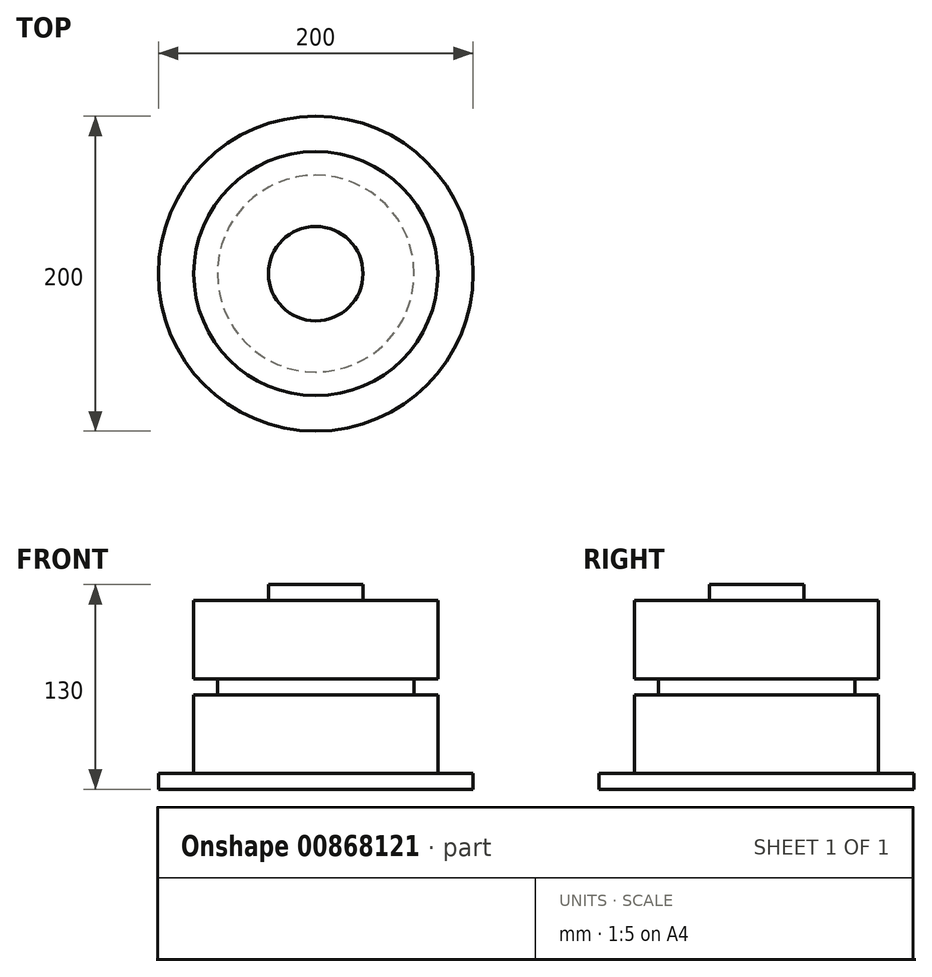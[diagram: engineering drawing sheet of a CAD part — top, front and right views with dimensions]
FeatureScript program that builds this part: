
annotation { "Feature Type Name" : "Feature", "Feature Type Description" : "" }
export const myFeature = defineFeature(function(context is Context, id is Id, definition is map)
    precondition{}
    {
        {
            var Q0;
            Q0=qCreatedBy(makeId("Front.planeOp"),FACE);
            var sketch = newSketch(context, id + "F0", { "sketchPlane" : qUnion([Q0])});
            skLineSegment(sketch, "E0", {"start": v(0, 0) * mm, "end": v(-30, 0) * mm});
            skLineSegment(sketch, "E1", {"start": v(-30, 0) * mm, "end": v(-30, -10) * mm});
            skLineSegment(sketch, "E2", {"start": v(-30, -10) * mm, "end": v(-77.5, -10) * mm});
            skLineSegment(sketch, "E3", {"start": v(-77.5, -10) * mm, "end": v(-77.5, -60) * mm});
            skLineSegment(sketch, "E4", {"start": v(-77.5, -60) * mm, "end": v(-62.5, -60) * mm});
            skLineSegment(sketch, "E5", {"start": v(-62.5, -60) * mm, "end": v(-62.5, -70) * mm});
            skLineSegment(sketch, "E6", {"start": v(-62.5, -70) * mm, "end": v(-77.5, -70) * mm});
            skLineSegment(sketch, "E7", {"start": v(-77.5, -70) * mm, "end": v(-77.5, -120) * mm});
            skLineSegment(sketch, "E8", {"start": v(0, -130) * mm, "end": v(0, 0) * mm});
            skLineSegment(sketch, "E9", {"start": v(-77.5, -120) * mm, "end": v(-100, -120) * mm});
            skLineSegment(sketch, "E10", {"start": v(-100, -120) * mm, "end": v(-100, -130) * mm});
            skLineSegment(sketch, "E11", {"start": v(-100, -130) * mm, "end": v(0, -130) * mm});
            skLineSegment(sketch, "E12", {"start": v(0, 45) * mm, "end": v(0, -182.47) * mm, "construction": true});
            skSolve(sketch);
        }
        {
            var Q0;
            Q0=makeQuery(id+"F0.imprint","IMPRINT",FACE,{"disambiguationData":[TD([[makeQuery(id+"F0.imprint","IMPRINT",EDGE,{"derivedFrom":sQuery(id+"F0.wireOp",EDGE,"E0")}),1.0]])]});
            var Q1;
            Q1=sQuery(id+"F0.wireOp",EDGE,"E12");
            revolve(context, id + "F1", {"surfaceOperationType" : NewSurfaceOperationType.NEW, "entities" : qUnion([Q0]), "axis" : qUnion([Q1]), "revolveType" : RevolveType.FULL});
        }
    });
